# Revit family: Sarlam_Lighting_LED_shaverlights__IP44_600_Lm
name_source: partatom
category: Dispositifs d'éclairage
units: mm (PartAtom-declared; Revit-internal decimal feet)

## family parameters
Conserver l'orientation des annotations = Oui
Cote de connecteur circulaire = Utiliser le diamètre
Couper avec des vides une fois chargée = Non
Hôte = Face
Partagée = Non
Point de calcul de pièce = Non
Type d'élément = Normal

## types (2) — shared parameters
Colour rendering index CRI = 0
Degree of protection (IP) = IP44
Effective luminous flux lm = 600
Elévation par défaut = 1800 mm
Fabricant = LEGRAND
General Conditions of Use = https://export.legrand.com
Impact strength (IK) = IK07
Lamp holder = 0
Light sharing = 0
Material housing = LEGRAND - Polycarbonate
Protection Class = II
Radiation angle = 0
Suitable for built-in mounting = Non
Suitable for ceiling mounting = Non
Suitable for surface mounting = Non
Suitable for suspended mounting = Non
Suitable for wall mounting = Non
Type of control gear = 0
URL = http://www.legrandoc.com
With light sensor = Non
With movement sensor = Non
zero-valued in all types: Built-in diameter, Built-in height/depth, Built-in length, Built-in width, Colour temperature K MAX, Colour temperature K MIN, Height/depth, Length, Nominal current mA MAX, Nominal current mA MIN, Nominal voltage (Un) V MAX, Nominal voltage (Un) V MIN, Outer diameter, System power W, Width

## per-type parameters (varying)
| type | Colour housing | Description | Modèle |
| ON/OFF | LEGRAND - Blanc | ECOLED 600LM IP44 | SL-189800 |
| Light switch | LEGRAND - White | ECOLED 600LM IP44 WITH SWITH | SL-189801 |

## geometry (parser evidence)
native form markers: Blend x10
no freeform markers — native parametric forms only
